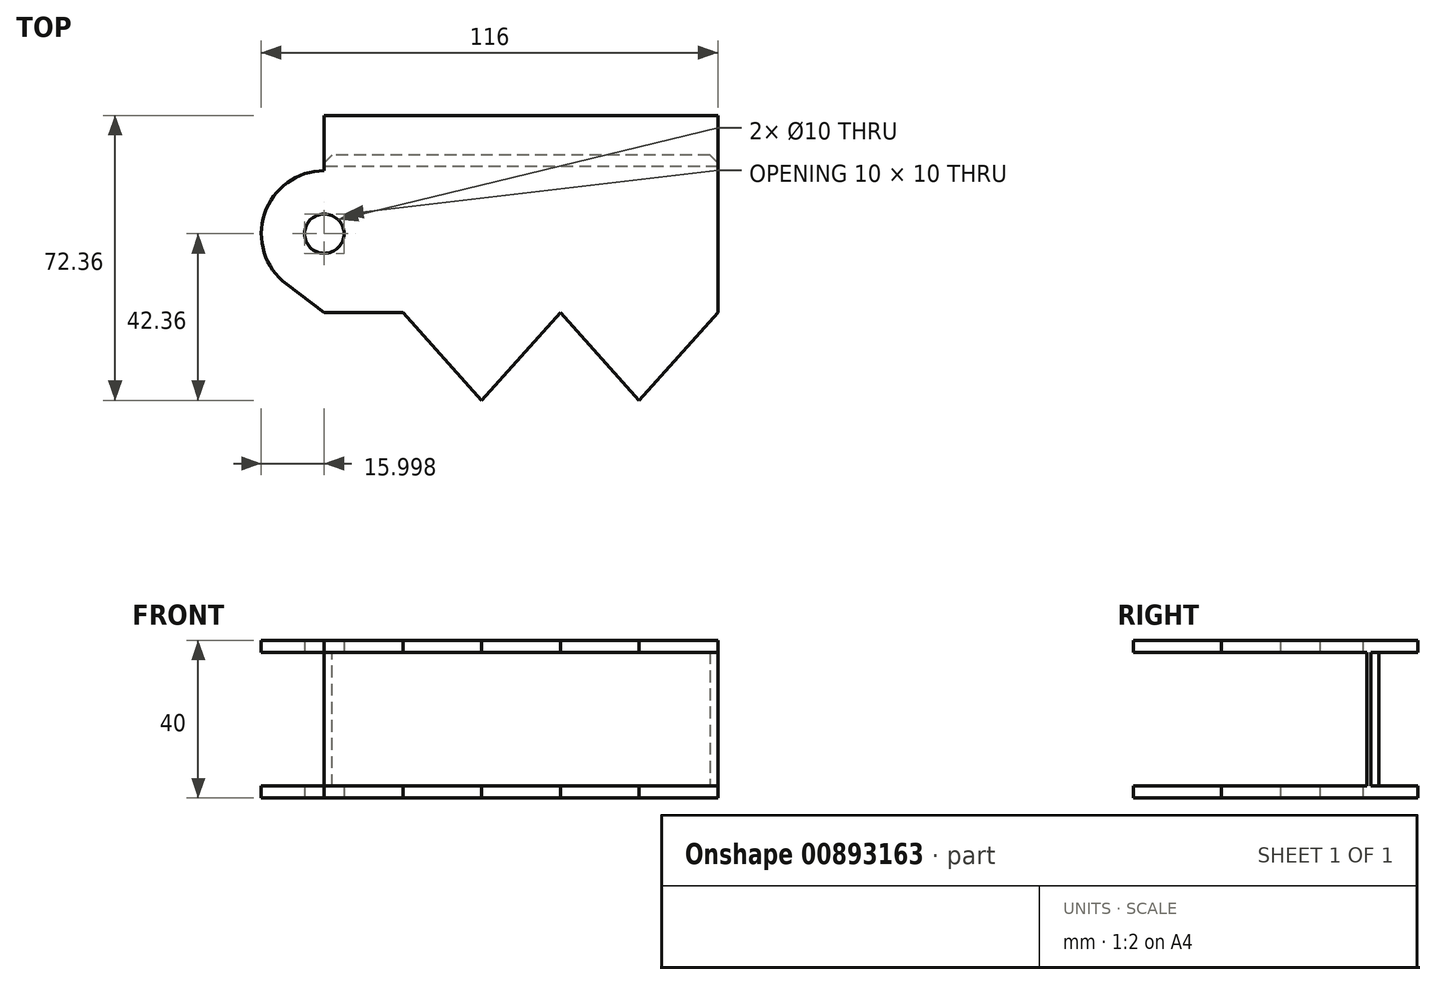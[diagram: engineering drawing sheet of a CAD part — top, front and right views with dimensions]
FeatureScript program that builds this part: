
annotation { "Feature Type Name" : "Feature", "Feature Type Description" : "" }
export const myFeature = defineFeature(function(context is Context, id is Id, definition is map)
    precondition{}
    {
        {
            var Q0;
            Q0=qCreatedBy(makeId("Top.planeOp"),FACE);
            var sketch = newSketch(context, id + "F0", { "sketchPlane" : qUnion([Q0])});
            skLineSegment(sketch, "E0", {"start": v(21.78, 56.67) * mm, "end": v(-78.22, 56.67) * mm});
            skLineSegment(sketch, "E1", {"start": v(-78.22, 56.67) * mm, "end": v(-78.22, 16.67) * mm});
            skPoint(sketch, "E2.startSnap0", {"position": v(41.78, 36.67) * mm});
            skCircle(sketch, "E3", {"center": v(21.78, 36.67) * mm, "radius": 5 * mm});
            skPoint(sketch, "E4.orphan", {"position": v(41.78, 56.67) * mm});
            skPoint(sketch, "E5.start.orphan", {"position": v(41.78, 16.67) * mm});
            skLineSegment(sketch, "E6", {"start": v(-18.22, -5.7) * mm, "end": v(-18.22, -7.75) * mm});
            skLineSegment(sketch, "E7", {"start": v(-38.22, 16.67) * mm, "end": v(-58.22, -5.7) * mm});
            skLineSegment(sketch, "E8", {"start": v(-58.22, -5.7) * mm, "end": v(-78.22, 16.67) * mm});
            skLineSegment(sketch, "E9", {"start": v(-38.22, 16.67) * mm, "end": v(-18.22, -5.7) * mm});
            skPoint(sketch, "E9.endSnap0", {"position": v(-18.22, -7.75) * mm});
            skLineSegment(sketch, "E10", {"start": v(-18.22, -5.7) * mm, "end": v(1.78, 16.67) * mm});
            skPoint(sketch, "E11.orphan", {"position": v(-18.22, -32.16) * mm});
            skLineSegment(sketch, "E12.trimOffspring", {"start": v(1.78, 16.67) * mm, "end": v(21.78, 16.67) * mm});
            skPoint(sketch, "E13.orphan", {"position": v(-18.22, 16.67) * mm});
            skArc(sketch, "E14", {"start": v(31.38, 23.87) * mm, "mid": v(36.96, 41.73) * mm, "end": v(21.78, 52.67) * mm});
            skLineSegment(sketch, "E15", {"start": v(21.78, 56.67) * mm, "end": v(21.78, 52.67) * mm});
            skLineSegment(sketch, "E16", {"start": v(21.78, 16.67) * mm, "end": v(31.38, 23.87) * mm});
            skSolve(sketch);
        }
        {
            var Q0;
            Q0 = qSketchRegion(id + "F0", true);
            extrude(context, id + "F1", {"entities" : qUnion([Q0]), "depth" : 40 * mm, "offsetDistance" : 25 * mm});
        }
        {
            var Q0;
            Q0=makeQuery(id+"F1.opExtrude","SWEPT_BODY",BODY,{"disambiguationData":[OSD([sQuery(id+"F0.wireOp",EDGE,"E0"),sQuery(id+"F0.wireOp",EDGE,"E1"),sQuery(id+"F0.wireOp",EDGE,"538490fa-0efd-4a56-b3e3-c0d5682f8158"),sQuery(id+"F0.wireOp",EDGE,"E3"),sQuery(id+"F0.wireOp",EDGE,"E7"),sQuery(id+"F0.wireOp",EDGE,"E8"),sQuery(id+"F0.wireOp",EDGE,"E9"),sQuery(id+"F0.wireOp",EDGE,"E10"),sQuery(id+"F0.wireOp",EDGE,"E12.trimOffspring")])]});
            transform(context, id + "F2", {"entities" : qUnion([Q0]), "transformType" : TransformType.TRANSLATION_3D, "dx" : 0 * mm, "dy" : 0 * mm, "dz" : 28 * mm, "makeCopy" : true});
        }
        {
            var Q0;
            Q0=makeQuery(id+"F2.opPattern","COPY",BODY,{"derivedFrom":makeQuery(id+"F1.opExtrude","SWEPT_BODY",BODY,{"disambiguationData":[OSD([sQuery(id+"F0.wireOp",EDGE,"E0"),sQuery(id+"F0.wireOp",EDGE,"E1"),sQuery(id+"F0.wireOp",EDGE,"538490fa-0efd-4a56-b3e3-c0d5682f8158"),sQuery(id+"F0.wireOp",EDGE,"E3"),sQuery(id+"F0.wireOp",EDGE,"E7"),sQuery(id+"F0.wireOp",EDGE,"E8"),sQuery(id+"F0.wireOp",EDGE,"E9"),sQuery(id+"F0.wireOp",EDGE,"E10"),sQuery(id+"F0.wireOp",EDGE,"E12.trimOffspring")])]}),"instanceName":"1"});
            deleteBodies(context, id + "F3", {"entities" : qUnion([Q0])});
        }
        {
            var Q0;
            Q0=makeQuery(id+"F1.opExtrude","SWEPT_BODY",BODY,{"disambiguationData":[OSD([sQuery(id+"F0.wireOp",EDGE,"E0"),sQuery(id+"F0.wireOp",EDGE,"E1"),sQuery(id+"F0.wireOp",EDGE,"538490fa-0efd-4a56-b3e3-c0d5682f8158"),sQuery(id+"F0.wireOp",EDGE,"E3"),sQuery(id+"F0.wireOp",EDGE,"E7"),sQuery(id+"F0.wireOp",EDGE,"E8"),sQuery(id+"F0.wireOp",EDGE,"E9"),sQuery(id+"F0.wireOp",EDGE,"E10"),sQuery(id+"F0.wireOp",EDGE,"E12.trimOffspring")])]});
            transform(context, id + "F4", {"entities" : qUnion([Q0]), "transformType" : TransformType.TRANSLATION_3D, "dx" : 0 * mm, "dy" : 0 * mm, "dz" : 34 * mm, "makeCopy" : true});
        }
        {
            var Q0;
            Q0=makeQuery(id+"F1.opExtrude","CAP_FACE",FACE,{"disambiguationData":[OSD([sQuery(id+"F0.wireOp",EDGE,"E0"),sQuery(id+"F0.wireOp",EDGE,"E1"),sQuery(id+"F0.wireOp",EDGE,"538490fa-0efd-4a56-b3e3-c0d5682f8158"),sQuery(id+"F0.wireOp",EDGE,"E3"),sQuery(id+"F0.wireOp",EDGE,"E7"),sQuery(id+"F0.wireOp",EDGE,"E8"),sQuery(id+"F0.wireOp",EDGE,"E9"),sQuery(id+"F0.wireOp",EDGE,"E10"),sQuery(id+"F0.wireOp",EDGE,"E12.trimOffspring")])],"isStart":false});
            var sketch = newSketch(context, id + "F5", { "sketchPlane" : qUnion([Q0])});
            skLineSegment(sketch, "E17", {"start": v(-78.22, 56.67) * mm, "end": v(-78.22, 53.67) * mm});
            skLineSegment(sketch, "E18", {"start": v(-78.22, 53.67) * mm, "end": v(21.78, 53.67) * mm});
            skLineSegment(sketch, "E19", {"start": v(21.78, 53.67) * mm, "end": v(21.78, 56.67) * mm});
            skLineSegment(sketch, "E20", {"start": v(21.78, 56.67) * mm, "end": v(-78.22, 56.67) * mm});
            skSolve(sketch);
        }
        {
            var Q0;
            Q0 = qSketchRegion(id + "F5", true);
            extrude(context, id + "F6", {"entities" : qUnion([Q0]), "depth" : 28 * mm, "offsetDistance" : 25 * mm});
        }
        {
            var Q0;
            Q0=makeQuery(id+"F6.opExtrude","SWEPT_FACE",FACE,{"disambiguationData":[OSD([sQuery(id+"F5.wireOp",EDGE,"E20")])]});
            var sketch = newSketch(context, id + "F7", { "sketchPlane" : qUnion([Q0])});
            skLineSegment(sketch, "E21", {"start": v(-21.78, 68) * mm, "end": v(-21.78, 71) * mm});
            skLineSegment(sketch, "E22", {"start": v(-21.78, 71) * mm, "end": v(78.22, 71) * mm});
            skLineSegment(sketch, "E23", {"start": v(78.22, 71) * mm, "end": v(78.22, 68) * mm});
            skLineSegment(sketch, "E24", {"start": v(78.22, 68) * mm, "end": v(-21.78, 68) * mm});
            skLineSegment(sketch, "E25", {"start": v(-21.78, 40) * mm, "end": v(78.22, 40) * mm});
            skLineSegment(sketch, "E26", {"start": v(78.22, 40) * mm, "end": v(78.22, 0) * mm});
            skLineSegment(sketch, "E27", {"start": v(78.22, 0) * mm, "end": v(-21.78, 0) * mm});
            skLineSegment(sketch, "E28", {"start": v(-21.78, 0) * mm, "end": v(-21.78, 40) * mm});
            skSolve(sketch);
        }
        {
            var Q0;
            Q0 = qSketchRegion(id + "F7", true);
            extrude(context, id + "F8", {"entities" : qUnion([Q0]), "depth" : 10 * mm, "offsetDistance" : 25 * mm});
        }
        {
            var Q0;
            Q0=makeQuery(id+"F4.opPattern","COPY",BODY,{"derivedFrom":makeQuery(id+"F1.opExtrude","SWEPT_BODY",BODY,{"disambiguationData":[OSD([sQuery(id+"F0.wireOp",EDGE,"E0"),sQuery(id+"F0.wireOp",EDGE,"E1"),sQuery(id+"F0.wireOp",EDGE,"538490fa-0efd-4a56-b3e3-c0d5682f8158"),sQuery(id+"F0.wireOp",EDGE,"E3"),sQuery(id+"F0.wireOp",EDGE,"E7"),sQuery(id+"F0.wireOp",EDGE,"E8"),sQuery(id+"F0.wireOp",EDGE,"E9"),sQuery(id+"F0.wireOp",EDGE,"E10"),sQuery(id+"F0.wireOp",EDGE,"E12.trimOffspring")])]}),"instanceName":"1"});
            deleteBodies(context, id + "F9", {"entities" : qUnion([Q0])});
        }
        {
            var Q0;
            Q0=makeQuery(id+"F6.opExtrude","SWEPT_BODY",BODY,{"disambiguationData":[OSD([sQuery(id+"F5.wireOp",EDGE,"E17"),sQuery(id+"F5.wireOp",EDGE,"E18"),sQuery(id+"F5.wireOp",EDGE,"E19"),sQuery(id+"F5.wireOp",EDGE,"E20")])]});
            deleteBodies(context, id + "F10", {"entities" : qUnion([Q0])});
        }
        {
            var Q0;
            Q0=makeQuery(id+"F8.opExtrude","SWEPT_BODY",BODY,{"disambiguationData":[OSD([sQuery(id+"F7.wireOp",EDGE,"E21"),sQuery(id+"F7.wireOp",EDGE,"E22"),sQuery(id+"F7.wireOp",EDGE,"E23"),sQuery(id+"F7.wireOp",EDGE,"E24")])]});
            var Q1;
            Q1=makeQuery(id+"F8.opExtrude","SWEPT_BODY",BODY,{"disambiguationData":[OSD([sQuery(id+"F7.wireOp",EDGE,"E25"),sQuery(id+"F7.wireOp",EDGE,"E26"),sQuery(id+"F7.wireOp",EDGE,"E27"),sQuery(id+"F7.wireOp",EDGE,"E28")])]});
            deleteBodies(context, id + "F11", {"entities" : qUnion([Q0, Q1])});
        }
        {
            var Q0;
            Q0=makeQuery(id+"F1.opExtrude","SWEPT_FACE",FACE,{"disambiguationData":[OSD([sQuery(id+"F0.wireOp",EDGE,"E1")])]});
            var sketch = newSketch(context, id + "F12", { "sketchPlane" : qUnion([Q0])});
            skLineSegment(sketch, "E29", {"start": v(-53.67, 30) * mm, "end": v(15.53, 30) * mm});
            skLineSegment(sketch, "E30", {"start": v(-53.67, 3) * mm, "end": v(13.7, 3) * mm});
            skLineSegment(sketch, "E31", {"start": v(13.7, 3) * mm, "end": v(15.53, 30) * mm});
            skLineSegment(sketch, "E32", {"start": v(-53.67, 3) * mm, "end": v(-53.67, 30) * mm});
            skSolve(sketch);
        }
        {
            var Q0;
            Q0 = qSketchRegion(id + "F12", true);
            extrude(context, id + "F13", {"entities" : qUnion([Q0]), "operationType" : NewBodyOperationType.REMOVE, "endBound" : BoundingType.THROUGH_ALL, "oppositeDirection" : true, "depth" : 25 * mm, "offsetDistance" : 25 * mm});
        }
        {
            var Q0;
            Q0=makeQuery(id+"F1.opExtrude","SWEPT_FACE",FACE,{"disambiguationData":[OSD([sQuery(id+"F0.wireOp",EDGE,"E0")])]});
            var sketch = newSketch(context, id + "F14", { "sketchPlane" : qUnion([Q0])});
            skLineSegment(sketch, "E33", {"start": v(-21.78, 0) * mm, "end": v(-21.78, 3) * mm});
            skLineSegment(sketch, "E34", {"start": v(-21.78, 3) * mm, "end": v(78.22, 3) * mm});
            skLineSegment(sketch, "E35", {"start": v(78.22, 3) * mm, "end": v(78.22, 0) * mm});
            skLineSegment(sketch, "E36", {"start": v(78.22, 0) * mm, "end": v(-21.78, 0) * mm});
            skLineSegment(sketch, "E37", {"start": v(-21.78, 40) * mm, "end": v(-21.78, 37) * mm});
            skLineSegment(sketch, "E38", {"start": v(-21.78, 37) * mm, "end": v(78.22, 37) * mm});
            skLineSegment(sketch, "E39", {"start": v(78.22, 37) * mm, "end": v(78.22, 40) * mm});
            skLineSegment(sketch, "E40", {"start": v(78.22, 40) * mm, "end": v(-21.78, 40) * mm});
            skSolve(sketch);
        }
        {
            var Q0;
            Q0 = qSketchRegion(id + "F14", true);
            extrude(context, id + "F15", {"entities" : qUnion([Q0]), "operationType" : NewBodyOperationType.ADD, "depth" : 10 * mm, "offsetDistance" : 25 * mm});
        }
        {
            var Q0;
            Q0=makeQuery(id+"F1.opExtrude","SWEPT_BODY",BODY,{"disambiguationData":[OSD([sQuery(id+"F0.wireOp",EDGE,"E0"),sQuery(id+"F0.wireOp",EDGE,"E1"),sQuery(id+"F0.wireOp",EDGE,"E3"),sQuery(id+"F0.wireOp",EDGE,"E7"),sQuery(id+"F0.wireOp",EDGE,"E8"),sQuery(id+"F0.wireOp",EDGE,"E9"),sQuery(id+"F0.wireOp",EDGE,"E10"),sQuery(id+"F0.wireOp",EDGE,"E12.trimOffspring"),sQuery(id+"F0.wireOp",EDGE,"E14"),sQuery(id+"F0.wireOp",EDGE,"E15"),sQuery(id+"F0.wireOp",EDGE,"E16")])]});
            var Q1;
            Q1=makeQuery(id+"F15.boolean.opBoolean","MERGE",FACE,{"derivedFrom":[makeQuery(id+"F1.opExtrude","SWEPT_FACE",FACE,{"disambiguationData":[OSD([sQuery(id+"F0.wireOp",EDGE,"E1")])]}),makeQuery(id+"F15.opExtrude","SWEPT_FACE",FACE,{"disambiguationData":[OSD([sQuery(id+"F14.wireOp",EDGE,"E35")])]}),makeQuery(id+"F15.opExtrude","SWEPT_FACE",FACE,{"disambiguationData":[OSD([sQuery(id+"F14.wireOp",EDGE,"E39")])]})]});
            mirror(context, id + "F16", {"operationType" : NewBodyOperationType.ADD, "entities" : qUnion([Q0]), "mirrorPlane" : qUnion([Q1])});
        }
        {
            var Q0;
            {var subQ0=makeQuery(id+"F15.boolean.opBoolean","MERGE",FACE,{"derivedFrom":[makeQuery(id+"F1.opExtrude","CAP_FACE",FACE,{"disambiguationData":[OSD([sQuery(id+"F0.wireOp",EDGE,"E0"),sQuery(id+"F0.wireOp",EDGE,"E1"),sQuery(id+"F0.wireOp",EDGE,"E3"),sQuery(id+"F0.wireOp",EDGE,"E7"),sQuery(id+"F0.wireOp",EDGE,"E8"),sQuery(id+"F0.wireOp",EDGE,"E9"),sQuery(id+"F0.wireOp",EDGE,"E10"),sQuery(id+"F0.wireOp",EDGE,"E12.trimOffspring"),sQuery(id+"F0.wireOp",EDGE,"E14"),sQuery(id+"F0.wireOp",EDGE,"E15"),sQuery(id+"F0.wireOp",EDGE,"E16")])],"isStart":false}),makeQuery(id+"F15.opExtrude","SWEPT_FACE",FACE,{"disambiguationData":[OSD([sQuery(id+"F14.wireOp",EDGE,"E40")])]})]});Q0=makeQuery(id+"F16.boolean.opBoolean","MERGE",FACE,{"derivedFrom":[subQ0,makeQuery(id+"F16.opPattern","COPY",FACE,{"derivedFrom":subQ0,"instanceName":"1"})]});}
            var sketch = newSketch(context, id + "F17", { "sketchPlane" : qUnion([Q0])});
            skLineSegment(sketch, "E41", {"start": v(-78.22, 16.67) * mm, "end": v(-78.22, 86.7) * mm});
            skLineSegment(sketch, "E42", {"start": v(-78.22, 86.7) * mm, "end": v(68.21, 86.7) * mm});
            skLineSegment(sketch, "E43", {"start": v(68.21, 86.7) * mm, "end": v(68.21, -27.72) * mm});
            skLineSegment(sketch, "E44", {"start": v(68.21, -27.72) * mm, "end": v(-78.22, -27.72) * mm});
            skLineSegment(sketch, "E45", {"start": v(-78.22, -27.72) * mm, "end": v(-78.22, 16.67) * mm});
            skSolve(sketch);
        }
        {
            var Q0;
            Q0 = qSketchRegion(id + "F17", true);
            extrude(context, id + "F18", {"entities" : qUnion([Q0]), "operationType" : NewBodyOperationType.REMOVE, "endBound" : BoundingType.THROUGH_ALL, "oppositeDirection" : true, "depth" : 25 * mm, "offsetDistance" : 25 * mm});
        }
        {
            var Q0;
            Q0=makeQuery(id+"F16.opPattern","COPY",EDGE,{"derivedFrom":makeQuery(id+"F1.opExtrude","SWEPT_EDGE",EDGE,{"disambiguationData":[OSD([sQuery(id+"F0.wireOp",EDGE,"E0"),sQuery(id+"F0.wireOp",EDGE,"E15")])]}),"instanceName":"1"});
            chamfer(context, id + "F19", {"entities" : qUnion([Q0]), "width" : 2 * mm, "tangentPropagation" : true});
        }
        {
            var Q0;
            {var subQ0=makeQuery(id+"F1.opExtrude","SWEPT_FACE",FACE,{"disambiguationData":[OSD([sQuery(id+"F0.wireOp",EDGE,"E0")])]});Q0=makeQuery(id+"F18.boolean.opBoolean","INTERSECT",EDGE,{"derivedFrom":[makeQuery(id+"F16.boolean.opBoolean","MERGE",FACE,{"derivedFrom":[subQ0,makeQuery(id+"F16.opPattern","COPY",FACE,{"derivedFrom":subQ0,"instanceName":"1"})]}),makeQuery(id+"F18.opExtrude","SWEPT_FACE",FACE,{"disambiguationData":[OSD([sQuery(id+"F17.wireOp",EDGE,"E41"),sQuery(id+"F17.wireOp",EDGE,"E45")])]})]});}
            chamfer(context, id + "F20", {"entities" : qUnion([Q0]), "width" : 2 * mm, "tangentPropagation" : true});
        }
        {
            var Q0;
            Q0=makeQuery(id+"F18.boolean.opBoolean","COPY",FACE,{"derivedFrom":makeQuery(id+"F18.opExtrude","SWEPT_FACE",FACE,{"disambiguationData":[OSD([sQuery(id+"F17.wireOp",EDGE,"E41"),sQuery(id+"F17.wireOp",EDGE,"E45")])]})});
            var sketch = newSketch(context, id + "F21", { "sketchPlane" : qUnion([Q0])});
            skLineSegment(sketch, "E46", {"start": v(53.67, 30) * mm, "end": v(53.67, 37) * mm});
            skLineSegment(sketch, "E47", {"start": v(53.67, 37) * mm, "end": v(-13.8, 37) * mm});
            skLineSegment(sketch, "E48", {"start": v(-13.8, 37) * mm, "end": v(-13.8, 30) * mm});
            skLineSegment(sketch, "E49", {"start": v(-13.8, 30) * mm, "end": v(53.67, 30) * mm});
            skSolve(sketch);
        }
        {
            var Q0;
            Q0 = qSketchRegion(id + "F21", true);
            extrude(context, id + "F22", {"entities" : qUnion([Q0]), "operationType" : NewBodyOperationType.REMOVE, "endBound" : BoundingType.THROUGH_ALL, "oppositeDirection" : true, "depth" : 25 * mm, "offsetDistance" : 25 * mm});
        }
    });
